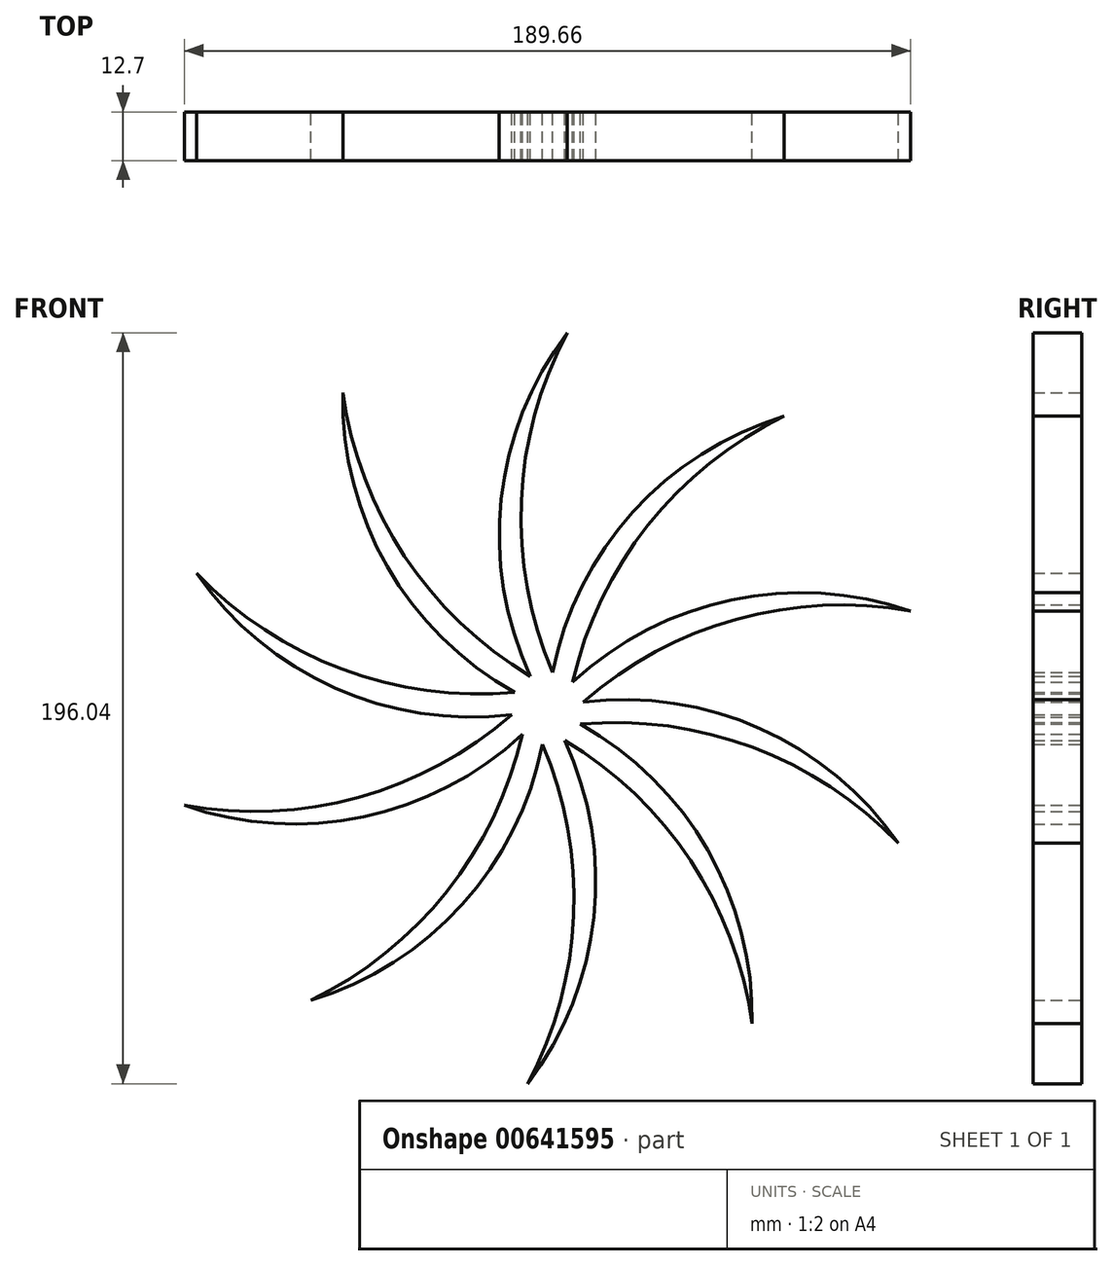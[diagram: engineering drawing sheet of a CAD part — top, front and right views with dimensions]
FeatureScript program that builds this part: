
annotation { "Feature Type Name" : "Feature", "Feature Type Description" : "" }
export const myFeature = defineFeature(function(context is Context, id is Id, definition is map)
    precondition{}
    {
        {
            var Q0;
            Q0=qCreatedBy(makeId("Front.planeOp"),FACE);
            var sketch = newSketch(context, id + "F0", { "sketchPlane" : qUnion([Q0])});
            skArc(sketch, "E0", {"start": v(61.81, 76.25) * mm, "mid": v(22.27, 51.22) * mm, "end": v(1.31, 9.37) * mm});
            skArc(sketch, "E1", {"start": v(61.81, 76.25) * mm, "mid": v(26.28, 47.83) * mm, "end": v(6.57, 6.81) * mm});
            skArc(sketch, "E2.1.0", {"start": v(5.19, 98.02) * mm, "mid": v(-6.85, 54.14) * mm, "end": v(1.31, 9.37) * mm});
            skArc(sketch, "E2.1.1", {"start": v(5.19, 98.02) * mm, "mid": v(-12.09, 54.53) * mm, "end": v(-4.45, 8.36) * mm});
            skArc(sketch, "E2.2.0", {"start": v(-53.42, 82.35) * mm, "mid": v(-37.37, 39.77) * mm, "end": v(-4.45, 8.36) * mm});
            skArc(sketch, "E2.2.1", {"start": v(-53.42, 82.35) * mm, "mid": v(-41.83, 37) * mm, "end": v(-8.5, 4.15) * mm});
            skPoint(sketch, "E2.center", {"position": v(0, 0) * mm});
            skArc(sketch, "E3.3.3.0", {"start": v(-91.62, 35.22) * mm, "mid": v(-53.6, 10.21) * mm, "end": v(-8.5, 4.15) * mm});
            skArc(sketch, "E3.4.3.0", {"start": v(-91.62, 35.22) * mm, "mid": v(-55.6, 5.36) * mm, "end": v(-9.32, -1.65) * mm});
            skArc(sketch, "E3.3.4.0", {"start": v(-94.83, -25.36) * mm, "mid": v(-49.37, -23.25) * mm, "end": v(-9.32, -1.65) * mm});
            skArc(sketch, "E3.4.4.0", {"start": v(-94.83, -25.36) * mm, "mid": v(-48.12, -28.34) * mm, "end": v(-6.57, -6.81) * mm});
            skArc(sketch, "E3.3.5.0", {"start": v(-61.81, -76.25) * mm, "mid": v(-26.28, -47.83) * mm, "end": v(-6.57, -6.81) * mm});
            skArc(sketch, "E3.4.5.0", {"start": v(-61.81, -76.25) * mm, "mid": v(-22.27, -51.22) * mm, "end": v(-1.31, -9.37) * mm});
            skArc(sketch, "E3.3.6.0", {"start": v(-5.19, -98.02) * mm, "mid": v(6.85, -54.14) * mm, "end": v(-1.31, -9.37) * mm});
            skArc(sketch, "E3.4.6.0", {"start": v(-5.19, -98.02) * mm, "mid": v(12.09, -54.53) * mm, "end": v(4.45, -8.36) * mm});
            skArc(sketch, "E3.3.7.0", {"start": v(53.42, -82.35) * mm, "mid": v(37.37, -39.77) * mm, "end": v(4.45, -8.36) * mm});
            skArc(sketch, "E3.4.7.0", {"start": v(53.42, -82.35) * mm, "mid": v(41.83, -37) * mm, "end": v(8.5, -4.15) * mm});
            skArc(sketch, "E3.3.8.0", {"start": v(91.62, -35.22) * mm, "mid": v(53.6, -10.21) * mm, "end": v(8.5, -4.15) * mm});
            skArc(sketch, "E3.4.8.0", {"start": v(91.62, -35.22) * mm, "mid": v(55.6, -5.36) * mm, "end": v(9.32, 1.65) * mm});
            skArc(sketch, "E3.3.9.0", {"start": v(94.83, 25.36) * mm, "mid": v(49.37, 23.25) * mm, "end": v(9.32, 1.65) * mm});
            skArc(sketch, "E3.4.9.0", {"start": v(94.83, 25.36) * mm, "mid": v(48.12, 28.34) * mm, "end": v(6.57, 6.81) * mm});
            skLineSegment(sketch, "E4", {"start": v(-5.26, 0) * mm, "end": v(-4.26, 3.1) * mm});
            skLineSegment(sketch, "E5", {"start": v(-4.26, 3.1) * mm, "end": v(-1.63, 5) * mm});
            skLineSegment(sketch, "E6", {"start": v(-1.63, 5) * mm, "end": v(1.63, 5) * mm});
            skLineSegment(sketch, "E7", {"start": v(1.63, 5) * mm, "end": v(4.26, 3.1) * mm});
            skLineSegment(sketch, "E8", {"start": v(4.26, 3.1) * mm, "end": v(5.26, 0) * mm});
            skLineSegment(sketch, "E9", {"start": v(5.26, 0) * mm, "end": v(4.26, -3.1) * mm});
            skLineSegment(sketch, "E10", {"start": v(4.26, -3.1) * mm, "end": v(1.63, -5) * mm});
            skLineSegment(sketch, "E11", {"start": v(1.63, -5) * mm, "end": v(-1.63, -5) * mm});
            skLineSegment(sketch, "E12", {"start": v(-1.63, -5) * mm, "end": v(-4.26, -3.1) * mm});
            skPoint(sketch, "E13.end.orphan", {"position": v(-5.05, 0) * mm});
            skLineSegment(sketch, "E14", {"start": v(-5.26, 0) * mm, "end": v(-4.26, -3.1) * mm});
            skArc(sketch, "E15.trimOffspring", {"start": v(-4.94, -1) * mm, "mid": v(-2.46, -0.54) * mm, "end": v(0, 0) * mm});
            skArc(sketch, "E16.trimOffspring", {"start": v(-4.58, 2.1) * mm, "mid": v(-2.3, 1.01) * mm, "end": v(0, 0) * mm});
            skArc(sketch, "E17.trimOffspring", {"start": v(-3.4, -3.71) * mm, "mid": v(-1.68, -1.88) * mm, "end": v(0, 0) * mm});
            skArc(sketch, "E18.trimOffspring", {"start": v(-0.57, -5) * mm, "mid": v(-0.25, -2.5) * mm, "end": v(0, 0) * mm});
            skArc(sketch, "E19.trimOffspring", {"start": v(2.48, -4.39) * mm, "mid": v(1.27, -2.18) * mm, "end": v(0, 0) * mm});
            skArc(sketch, "E20.trimOffspring", {"start": v(4.58, -2.1) * mm, "mid": v(2.3, -1.01) * mm, "end": v(0, 0) * mm});
            skArc(sketch, "E21.trimOffspring", {"start": v(4.94, 1) * mm, "mid": v(2.46, 0.54) * mm, "end": v(0, 0) * mm});
            skArc(sketch, "E22.trimOffspring", {"start": v(3.4, 3.71) * mm, "mid": v(1.68, 1.88) * mm, "end": v(0, 0) * mm});
            skArc(sketch, "E23.trimOffspring", {"start": v(-2.48, 4.39) * mm, "mid": v(-1.27, 2.18) * mm, "end": v(0, 0) * mm});
            skArc(sketch, "E24.trimOffspring", {"start": v(0.57, 5) * mm, "mid": v(0.25, 2.5) * mm, "end": v(0, 0) * mm});
            skSolve(sketch);
        }
        {
            var Q0;
            Q0=makeQuery(id+"F0.imprint","IMPRINT",FACE,{"disambiguationData":[TD([[makeQuery(id+"F0.imprint","IMPRINT",EDGE,{"derivedFrom":sQuery(id+"F0.wireOp",EDGE,"E0")}),1.0]])]});
            var Q1;
            {var subQ4=sQuery(id+"F0.wireOp",EDGE,"E17.trimOffspring");Q1=makeQuery(id+"F0.imprint","IMPRINT",FACE,{"disambiguationData":[TD([[makeQuery(id+"F0.imprint","IMPRINT",EDGE,{"derivedFrom":subQ4}),-1.0]])]});}
            var Q2;
            {var subQ4=sQuery(id+"F0.wireOp",EDGE,"E15.trimOffspring");Q2=makeQuery(id+"F0.imprint","IMPRINT",FACE,{"disambiguationData":[TD([[makeQuery(id+"F0.imprint","IMPRINT",EDGE,{"derivedFrom":subQ4}),-1.0]])]});}
            var Q3;
            {var subQ4=sQuery(id+"F0.wireOp",EDGE,"E15.trimOffspring");Q3=makeQuery(id+"F0.imprint","IMPRINT",FACE,{"disambiguationData":[TD([[makeQuery(id+"F0.imprint","IMPRINT",EDGE,{"derivedFrom":subQ4}),1.0]])]});}
            var Q4;
            {var subQ3=sQuery(id+"F0.wireOp",EDGE,"E16.trimOffspring");Q4=makeQuery(id+"F0.imprint","IMPRINT",FACE,{"disambiguationData":[TD([[makeQuery(id+"F0.imprint","IMPRINT",EDGE,{"derivedFrom":subQ3}),1.0]])]});}
            var Q5;
            {var subQ3=sQuery(id+"F0.wireOp",EDGE,"E23.trimOffspring");Q5=makeQuery(id+"F0.imprint","IMPRINT",FACE,{"disambiguationData":[TD([[makeQuery(id+"F0.imprint","IMPRINT",EDGE,{"derivedFrom":subQ3}),1.0]])]});}
            var Q6;
            {var subQ4=sQuery(id+"F0.wireOp",EDGE,"E22.trimOffspring");Q6=makeQuery(id+"F0.imprint","IMPRINT",FACE,{"disambiguationData":[TD([[makeQuery(id+"F0.imprint","IMPRINT",EDGE,{"derivedFrom":subQ4}),-1.0]])]});}
            var Q7;
            {var subQ4=sQuery(id+"F0.wireOp",EDGE,"E21.trimOffspring");Q7=makeQuery(id+"F0.imprint","IMPRINT",FACE,{"disambiguationData":[TD([[makeQuery(id+"F0.imprint","IMPRINT",EDGE,{"derivedFrom":subQ4}),-1.0]])]});}
            var Q8;
            {var subQ4=sQuery(id+"F0.wireOp",EDGE,"E20.trimOffspring");Q8=makeQuery(id+"F0.imprint","IMPRINT",FACE,{"disambiguationData":[TD([[makeQuery(id+"F0.imprint","IMPRINT",EDGE,{"derivedFrom":subQ4}),-1.0]])]});}
            var Q9;
            {var subQ4=sQuery(id+"F0.wireOp",EDGE,"E19.trimOffspring");Q9=makeQuery(id+"F0.imprint","IMPRINT",FACE,{"disambiguationData":[TD([[makeQuery(id+"F0.imprint","IMPRINT",EDGE,{"derivedFrom":subQ4}),-1.0]])]});}
            var Q10;
            {var subQ4=sQuery(id+"F0.wireOp",EDGE,"E18.trimOffspring");Q10=makeQuery(id+"F0.imprint","IMPRINT",FACE,{"disambiguationData":[TD([[makeQuery(id+"F0.imprint","IMPRINT",EDGE,{"derivedFrom":subQ4}),-1.0]])]});}
            extrude(context, id + "F1", {"entities" : qUnion([Q0, Q1, Q2, Q3, Q4, Q5, Q6, Q7, Q8, Q9, Q10]), "depth" : 12.7 * mm, "offsetDistance" : 25.4 * mm});
        }
    });
